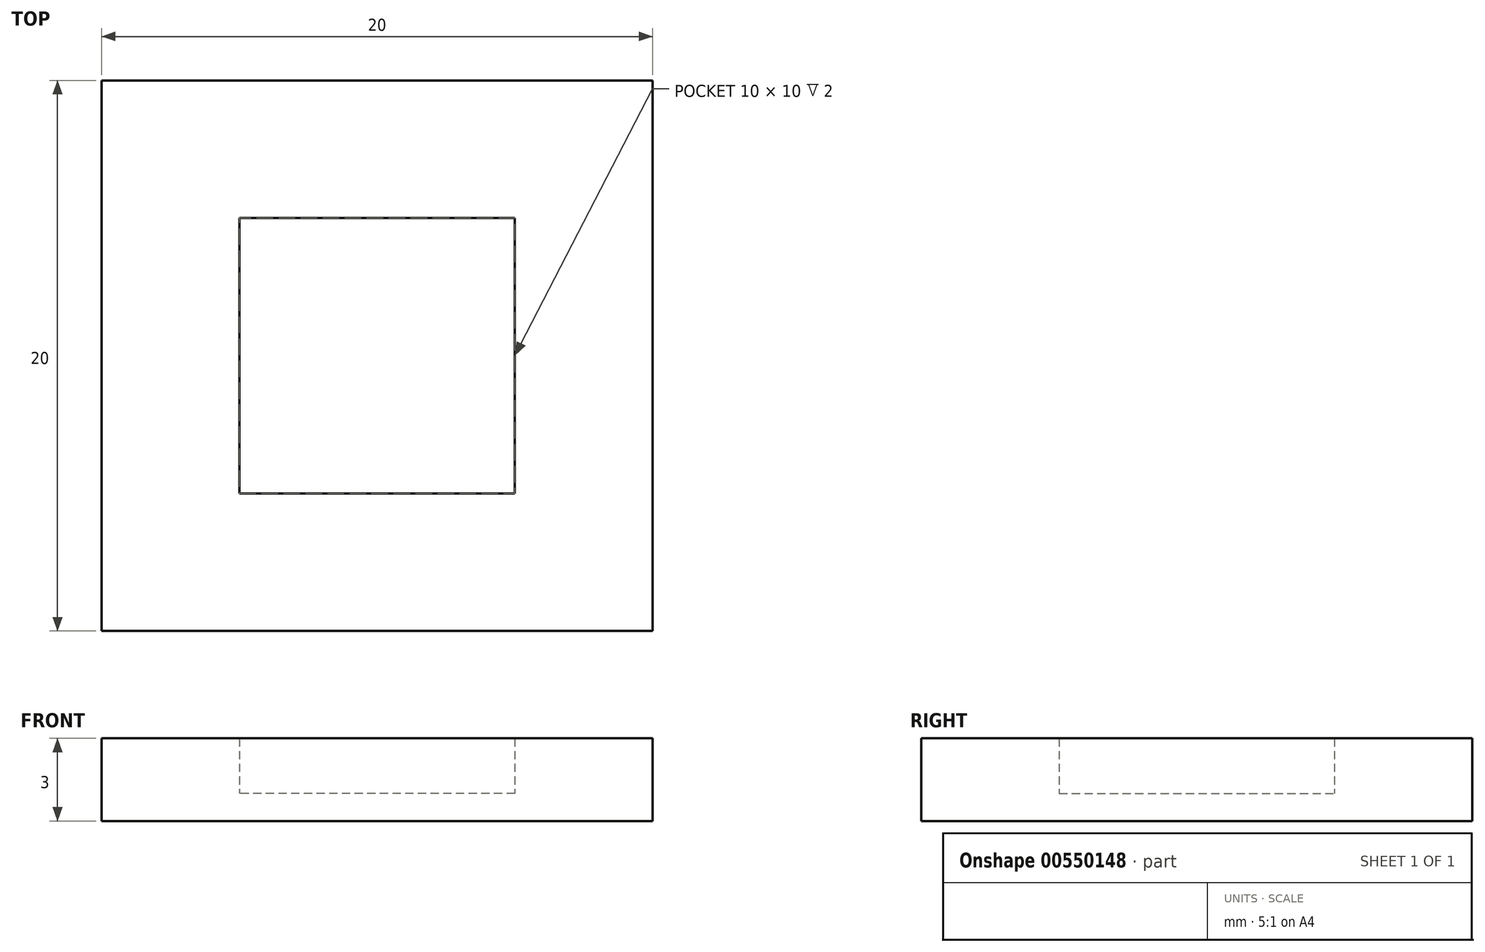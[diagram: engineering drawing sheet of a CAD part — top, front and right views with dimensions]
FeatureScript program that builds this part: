
annotation { "Feature Type Name" : "Feature", "Feature Type Description" : "" }
export const myFeature = defineFeature(function(context is Context, id is Id, definition is map)
    precondition{}
    {
        {
            var Q0;
            Q0=qCreatedBy(makeId("Top.planeOp"),FACE);
            var sketch = newSketch(context, id + "F0", { "sketchPlane" : qUnion([Q0])});
            skLineSegment(sketch, "E0.bottom", {"start": v(10, -10) * mm, "end": v(-10, -10) * mm});
            skLineSegment(sketch, "E0.top", {"start": v(10, 10) * mm, "end": v(-10, 10) * mm});
            skLineSegment(sketch, "E0.left", {"start": v(10, -10) * mm, "end": v(10, 10) * mm});
            skLineSegment(sketch, "E0.right", {"start": v(-10, -10) * mm, "end": v(-10, 10) * mm});
            skLineSegment(sketch, "E1.0", {"start": v(5, -5) * mm, "end": v(5, 5) * mm});
            skLineSegment(sketch, "E1.1", {"start": v(5, -5) * mm, "end": v(-5, -5) * mm});
            skLineSegment(sketch, "E1.2", {"start": v(-5, -5) * mm, "end": v(-5, 5) * mm});
            skLineSegment(sketch, "E1.3", {"start": v(5, 5) * mm, "end": v(-5, 5) * mm});
            skSolve(sketch);
        }
        {
            var Q0;
            Q0=makeQuery(id+"F0.imprint","IMPRINT",FACE,{"disambiguationData":[TD([[makeQuery(id+"F0.imprint","IMPRINT",EDGE,{"derivedFrom":sQuery(id+"F0.wireOp",EDGE,"E1.0")}),1.0]])]});
            extrude(context, id + "F1", {"entities" : qUnion([Q0]), "depth" : 1 * mm, "offsetDistance" : 25 * mm});
        }
        {
            var Q0;
            Q0=makeQuery(id+"F0.imprint","IMPRINT",FACE,{"disambiguationData":[TD([[makeQuery(id+"F0.imprint","IMPRINT",EDGE,{"derivedFrom":sQuery(id+"F0.wireOp",EDGE,"E0.bottom")}),-1.0]])]});
            extrude(context, id + "F2", {"entities" : qUnion([Q0]), "operationType" : NewBodyOperationType.ADD, "depth" : 3 * mm, "offsetDistance" : 25 * mm});
        }
    });
